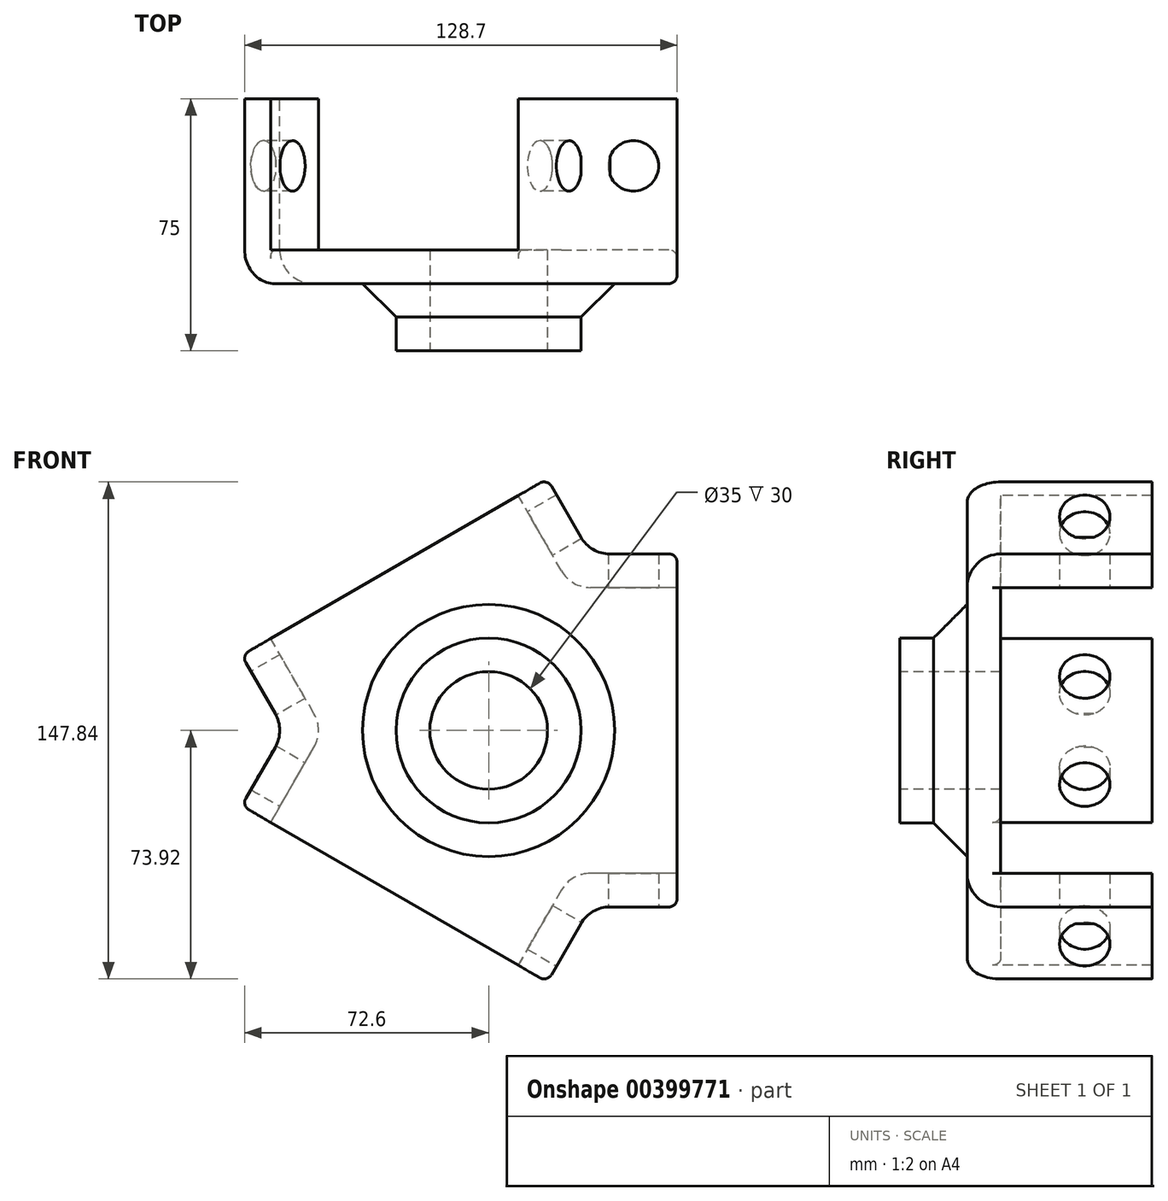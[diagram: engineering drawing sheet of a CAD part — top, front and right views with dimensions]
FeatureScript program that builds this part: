
annotation { "Feature Type Name" : "Feature", "Feature Type Description" : "" }
export const myFeature = defineFeature(function(context is Context, id is Id, definition is map)
    precondition{}
    {
        {
            var Q0;
            Q0=qCreatedBy(makeId("Front.planeOp"),FACE);
            var sketch = newSketch(context, id + "F0", { "sketchPlane" : qUnion([Q0])});
            skCircle(sketch, "E0", {"center": v(0, 0) * mm, "radius": 27.5 * mm});
            skCircle(sketch, "E1", {"center": v(0, 0) * mm, "radius": 17.5 * mm});
            skSolve(sketch);
        }
        {
            var Q0;
            Q0=makeQuery(id+"F0.imprint","IMPRINT",FACE,{"disambiguationData":[TD([[makeQuery(id+"F0.imprint","IMPRINT",EDGE,{"derivedFrom":sQuery(id+"F0.wireOp",EDGE,"E1")}),1.0]])]});
            var Q1;
            Q1=makeQuery(id+"F0.imprint","IMPRINT",FACE,{"disambiguationData":[TD([[makeQuery(id+"F0.imprint","IMPRINT",EDGE,{"derivedFrom":sQuery(id+"F0.wireOp",EDGE,"E0")}),1.0]])]});
            extrude(context, id + "F1", {"entities" : qUnion([Q0, Q1]), "oppositeDirection" : true, "depth" : 10 * mm});
        }
        {
            var Q0;
            Q0=makeQuery(id+"F1.opExtrude","CAP_FACE",FACE,{"disambiguationData":[OSD([sQuery(id+"F0.wireOp",EDGE,"E0"),sQuery(id+"F0.wireOp",EDGE,"E1")])],"isStart":false});
            cPlane(context, id + "F2", {"entities" : qUnion([Q0]), "cplaneType" : CPlaneType.OFFSET, "offset" : 10 * mm, "width" : 152.4 * mm, "height" : 152.4 * mm});
        }
        {
            var Q0;
            Q0=qCreatedBy(id+"F2.planeOp",FACE);
            var sketch = newSketch(context, id + "F3", { "sketchPlane" : qUnion([Q0])});
            skCircle(sketch, "E2", {"center": v(0, 0) * mm, "radius": 37.5 * mm});
            skSolve(sketch);
        }
        {
            var Q0;
            Q0=makeQuery(id+"F1.opExtrude","CAP_FACE",FACE,{"disambiguationData":[OSD([sQuery(id+"F0.wireOp",EDGE,"E0"),sQuery(id+"F0.wireOp",EDGE,"E1")])],"isStart":false});
            var sketch = newSketch(context, id + "F4", { "sketchPlane" : qUnion([Q0])});
            skCircle(sketch, "E3.0", {"center": v(0, 0) * mm, "radius": 27.5 * mm});
            skSolve(sketch);
        }
        {
            var Q1;
            Q1=makeQuery(id+"F4.imprint","IMPRINT",FACE,{"disambiguationData":[TD([[makeQuery(id+"F4.imprint","IMPRINT",EDGE,{"derivedFrom":sQuery(id+"F4.wireOp",EDGE,"E3.0")}),-1.0]])]});
            var Q2;
            Q2=makeQuery(id+"F3.imprint","IMPRINT",FACE,{"disambiguationData":[TD([[makeQuery(id+"F3.imprint","IMPRINT",EDGE,{"derivedFrom":sQuery(id+"F3.wireOp",EDGE,"E2")}),1.0]])]});
            loft(context, id + "F5", {"operationType" : NewBodyOperationType.ADD, "sheetProfilesArray" : [{ "sheetProfileEntities" : qUnion([Q1]) }, { "sheetProfileEntities" : qUnion([Q2]) }]});
        }
        {
            var Q0;
            Q0=makeQuery(id+"F5.opLoft","CAP_FACE",FACE,{"disambiguationData":[OSD([makeQuery(id+"F3.imprint","IMPRINT",FACE,{"disambiguationData":[TD([[makeQuery(id+"F3.imprint","IMPRINT",EDGE,{"derivedFrom":sQuery(id+"F3.wireOp",EDGE,"E2")}),1.0]])]})])],"isStart":true});
            var sketch = newSketch(context, id + "F6", { "sketchPlane" : qUnion([Q0])});
            skLineSegment(sketch, "E4", {"start": v(-103.3, 0) * mm, "end": v(129.97, 0) * mm, "construction": true});
            skLineSegment(sketch, "E5", {"start": v(0, 59.82) * mm, "end": v(0, -72.01) * mm, "construction": true});
            skLineSegment(sketch, "E6", {"start": v(-56.1, 52.5) * mm, "end": v(-56.1, -52.5) * mm});
            skLineSegment(sketch, "E7", {"start": v(-56.1, 52.5) * mm, "end": v(-30.31, 52.5) * mm});
            skLineSegment(sketch, "E8", {"start": v(-30.31, 52.5) * mm, "end": v(-17.42, 74.83) * mm});
            skLineSegment(sketch, "E9", {"start": v(-17.42, 74.83) * mm, "end": v(73.52, 22.33) * mm});
            skLineSegment(sketch, "E10", {"start": v(73.52, 22.33) * mm, "end": v(60.62, 0) * mm});
            skLineSegment(sketch, "E11", {"start": v(60.62, 0) * mm, "end": v(73.52, -22.33) * mm});
            skLineSegment(sketch, "E12", {"start": v(73.52, -22.33) * mm, "end": v(-17.42, -74.83) * mm});
            skLineSegment(sketch, "E13", {"start": v(-17.42, -74.83) * mm, "end": v(-30.31, -52.5) * mm});
            skLineSegment(sketch, "E14", {"start": v(-30.31, -52.5) * mm, "end": v(-56.1, -52.5) * mm});
            skSolve(sketch);
        }
        {
            var Q0;
            Q0 = qSketchRegion(id + "F6", true);
            extrude(context, id + "F7", {"entities" : qUnion([Q0]), "operationType" : NewBodyOperationType.ADD, "depth" : 10 * mm});
        }
        {
            var Q0;
            Q0=makeQuery(id+"F7.opExtrude","CAP_FACE",FACE,{"disambiguationData":[OSD([sQuery(id+"F6.wireOp",EDGE,"E6"),sQuery(id+"F6.wireOp",EDGE,"E7"),sQuery(id+"F6.wireOp",EDGE,"E8"),sQuery(id+"F6.wireOp",EDGE,"E9"),sQuery(id+"F6.wireOp",EDGE,"E10"),sQuery(id+"F6.wireOp",EDGE,"E11"),sQuery(id+"F6.wireOp",EDGE,"E12"),sQuery(id+"F6.wireOp",EDGE,"E13"),sQuery(id+"F6.wireOp",EDGE,"E14")])],"isStart":false});
            var sketch = newSketch(context, id + "F8", { "sketchPlane" : qUnion([Q0])});
            skLineSegment(sketch, "E15", {"start": v(-56.1, 52.5) * mm, "end": v(-56.1, 42.5) * mm});
            skLineSegment(sketch, "E16", {"start": v(-56.1, 42.5) * mm, "end": v(-24.54, 42.5) * mm});
            skLineSegment(sketch, "E17", {"start": v(-30.31, 52.5) * mm, "end": v(-56.1, 52.5) * mm});
            skLineSegment(sketch, "E18", {"start": v(-24.54, 42.5) * mm, "end": v(-8.76, 69.83) * mm});
            skLineSegment(sketch, "E19", {"start": v(-8.76, 69.83) * mm, "end": v(-17.42, 74.83) * mm});
            skLineSegment(sketch, "E20", {"start": v(-17.42, 74.83) * mm, "end": v(-30.31, 52.5) * mm});
            skLineSegment(sketch, "E21", {"start": v(-56.1, -52.5) * mm, "end": v(-56.1, -42.5) * mm});
            skLineSegment(sketch, "E22", {"start": v(-56.1, -42.5) * mm, "end": v(-24.54, -42.5) * mm});
            skLineSegment(sketch, "E23", {"start": v(-24.54, -42.5) * mm, "end": v(-8.76, -69.83) * mm});
            skLineSegment(sketch, "E24", {"start": v(-8.76, -69.83) * mm, "end": v(-17.42, -74.83) * mm});
            skLineSegment(sketch, "E25", {"start": v(-17.42, -74.83) * mm, "end": v(-30.31, -52.5) * mm});
            skLineSegment(sketch, "E26", {"start": v(-30.31, -52.5) * mm, "end": v(-56.1, -52.5) * mm});
            skLineSegment(sketch, "E27", {"start": v(73.52, -22.33) * mm, "end": v(64.86, -27.33) * mm});
            skLineSegment(sketch, "E28", {"start": v(64.86, -27.33) * mm, "end": v(49.07, 0) * mm});
            skLineSegment(sketch, "E29", {"start": v(49.07, 0) * mm, "end": v(64.86, 27.33) * mm});
            skLineSegment(sketch, "E30", {"start": v(64.86, 27.33) * mm, "end": v(73.52, 22.33) * mm});
            skLineSegment(sketch, "E31", {"start": v(73.52, 22.33) * mm, "end": v(60.62, 0) * mm});
            skLineSegment(sketch, "E32", {"start": v(60.62, 0) * mm, "end": v(73.52, -22.33) * mm});
            skLineSegment(sketch, "E33", {"start": v(64.86, -27.33) * mm, "end": v(73.52, -22.33) * mm});
            skSolve(sketch);
        }
        {
            var Q0;
            Q0 = qSketchRegion(id + "F8", true);
            extrude(context, id + "F9", {"entities" : qUnion([Q0]), "operationType" : NewBodyOperationType.ADD, "depth" : 45 * mm});
        }
        {
            var Q0;
            Q0=makeQuery(id+"F9.boolean.opBoolean","MERGE",EDGE,{"derivedFrom":[makeQuery(id+"F7.opExtrude","SWEPT_EDGE",EDGE,{"disambiguationData":[OSD([sQuery(id+"F6.wireOp",EDGE,"E10"),sQuery(id+"F6.wireOp",EDGE,"E11")])]}),makeQuery(id+"F9.opExtrude","SWEPT_EDGE",EDGE,{"disambiguationData":[OSD([sQuery(id+"F8.wireOp",EDGE,"E31"),sQuery(id+"F8.wireOp",EDGE,"E32")])]})]});
            var Q1;
            Q1=makeQuery(id+"F9.boolean.opBoolean","MERGE",EDGE,{"derivedFrom":[makeQuery(id+"F7.opExtrude","SWEPT_EDGE",EDGE,{"disambiguationData":[OSD([sQuery(id+"F6.wireOp",EDGE,"E7"),sQuery(id+"F6.wireOp",EDGE,"E8")])]}),makeQuery(id+"F9.opExtrude","SWEPT_EDGE",EDGE,{"disambiguationData":[OSD([sQuery(id+"F8.wireOp",EDGE,"E17"),sQuery(id+"F8.wireOp",EDGE,"E20")])]})]});
            var Q2;
            Q2=makeQuery(id+"F9.boolean.opBoolean","MERGE",EDGE,{"derivedFrom":[makeQuery(id+"F7.opExtrude","SWEPT_EDGE",EDGE,{"disambiguationData":[OSD([sQuery(id+"F6.wireOp",EDGE,"E13"),sQuery(id+"F6.wireOp",EDGE,"E14")])]}),makeQuery(id+"F9.opExtrude","SWEPT_EDGE",EDGE,{"disambiguationData":[OSD([sQuery(id+"F8.wireOp",EDGE,"E25"),sQuery(id+"F8.wireOp",EDGE,"E26")])]})]});
            var Q3;
            Q3=makeQuery(id+"F9.opExtrude","SWEPT_EDGE",EDGE,{"disambiguationData":[OSD([sQuery(id+"F8.wireOp",EDGE,"E22"),sQuery(id+"F8.wireOp",EDGE,"E23")])]});
            var Q4;
            Q4=makeQuery(id+"F9.opExtrude","SWEPT_EDGE",EDGE,{"disambiguationData":[OSD([sQuery(id+"F8.wireOp",EDGE,"E28"),sQuery(id+"F8.wireOp",EDGE,"E29")])]});
            var Q5;
            Q5=makeQuery(id+"F9.opExtrude","SWEPT_EDGE",EDGE,{"disambiguationData":[OSD([sQuery(id+"F8.wireOp",EDGE,"E16"),sQuery(id+"F8.wireOp",EDGE,"E18")])]});
            var Q6;
            Q6=makeQuery(id+"F9.opExtrude","CAP_EDGE",EDGE,{"disambiguationData":[OSD([sQuery(id+"F8.wireOp",EDGE,"E18")])],"isStart":true});
            var Q7;
            Q7=makeQuery(id+"F9.opExtrude","CAP_EDGE",EDGE,{"disambiguationData":[OSD([sQuery(id+"F8.wireOp",EDGE,"E23")])],"isStart":true});
            fillet(context, id + "F10", {"entities" : qUnion([Q0, Q1, Q2, Q3, Q4, Q5, Q6, Q7]), "radius" : 10 * mm, "tangentPropagation" : true, "allowEdgeOverflow" : false});
        }
        {
            var Q0;
            Q0=makeQuery(id+"F9.opExtrude","CAP_EDGE",EDGE,{"disambiguationData":[OSD([sQuery(id+"F8.wireOp",EDGE,"E29")])],"isStart":true});
            var Q1;
            Q1=makeQuery(id+"F7.opExtrude","CAP_EDGE",EDGE,{"disambiguationData":[OSD([sQuery(id+"F6.wireOp",EDGE,"E11")])],"isStart":true});
            var Q2;
            Q2=makeQuery(id+"F7.opExtrude","CAP_EDGE",EDGE,{"disambiguationData":[OSD([sQuery(id+"F6.wireOp",EDGE,"E13")])],"isStart":true});
            var Q3;
            Q3=makeQuery(id+"F7.opExtrude","CAP_EDGE",EDGE,{"disambiguationData":[OSD([sQuery(id+"F6.wireOp",EDGE,"E8")])],"isStart":true});
            fillet(context, id + "F11", {"entities" : qUnion([Q0, Q1, Q2, Q3]), "radius" : 10 * mm, "tangentPropagation" : true, "allowEdgeOverflow" : false});
        }
        {
            var Q0;
            Q0=makeQuery(id+"F7.opExtrude","CAP_EDGE",EDGE,{"disambiguationData":[OSD([sQuery(id+"F6.wireOp",EDGE,"E9")])],"isStart":true});
            var Q1;
            Q1=makeQuery(id+"F11.opFillet","BLEND_EDGE",EDGE,{"blendedFrom":[makeQuery(id+"F9.opExtrude","CAP_EDGE",EDGE,{"disambiguationData":[OSD([sQuery(id+"F8.wireOp",EDGE,"E29")])],"isStart":true}),makeQuery(id+"F9.boolean.opBoolean","MERGE",FACE,{"derivedFrom":[makeQuery(id+"F7.opExtrude","SWEPT_FACE",FACE,{"disambiguationData":[OSD([sQuery(id+"F6.wireOp",EDGE,"E9")])]}),makeQuery(id+"F9.opExtrude","SWEPT_FACE",FACE,{"disambiguationData":[OSD([sQuery(id+"F8.wireOp",EDGE,"E19")])]}),makeQuery(id+"F9.opExtrude","SWEPT_FACE",FACE,{"disambiguationData":[OSD([sQuery(id+"F8.wireOp",EDGE,"E30")])]})]})],"blendedInto":[makeQuery(id+"F9.boolean.opBoolean","MERGE",FACE,{"derivedFrom":[makeQuery(id+"F7.opExtrude","SWEPT_FACE",FACE,{"disambiguationData":[OSD([sQuery(id+"F6.wireOp",EDGE,"E9")])]}),makeQuery(id+"F9.opExtrude","SWEPT_FACE",FACE,{"disambiguationData":[OSD([sQuery(id+"F8.wireOp",EDGE,"E19")])]}),makeQuery(id+"F9.opExtrude","SWEPT_FACE",FACE,{"disambiguationData":[OSD([sQuery(id+"F8.wireOp",EDGE,"E30")])]})]})]});
            var Q2;
            Q2=makeQuery(id+"F7.opExtrude","CAP_EDGE",EDGE,{"disambiguationData":[OSD([sQuery(id+"F6.wireOp",EDGE,"E12")])],"isStart":true});
            var Q3;
            Q3=makeQuery(id+"F7.opExtrude","CAP_EDGE",EDGE,{"disambiguationData":[OSD([sQuery(id+"F6.wireOp",EDGE,"E12")])],"isStart":false});
            var Q4;
            Q4=makeQuery(id+"F7.opExtrude","CAP_EDGE",EDGE,{"disambiguationData":[OSD([sQuery(id+"F6.wireOp",EDGE,"E6")])],"isStart":false});
            var Q5;
            Q5=makeQuery(id+"F7.opExtrude","CAP_EDGE",EDGE,{"disambiguationData":[OSD([sQuery(id+"F6.wireOp",EDGE,"E6")])],"isStart":true});
            fillet(context, id + "F12", {"entities" : qUnion([Q0, Q1, Q2, Q3, Q4, Q5]), "radius" : 2.5 * mm, "tangentPropagation" : true, "allowEdgeOverflow" : false});
        }
        {
            var Q0;
            Q0=makeQuery(id+"F0.imprint","IMPRINT",FACE,{"disambiguationData":[TD([[makeQuery(id+"F0.imprint","IMPRINT",EDGE,{"derivedFrom":sQuery(id+"F0.wireOp",EDGE,"E1")}),1.0]])]});
            extrude(context, id + "F13", {"entities" : qUnion([Q0]), "operationType" : NewBodyOperationType.REMOVE, "oppositeDirection" : true, "depth" : 69.6 * mm});
        }
        {
            var Q0;
            Q0=makeQuery(id+"F9.opExtrude","SWEPT_FACE",FACE,{"disambiguationData":[OSD([sQuery(id+"F8.wireOp",EDGE,"E18")])]});
            var sketch = newSketch(context, id + "F14", { "sketchPlane" : qUnion([Q0])});
            skCircle(sketch, "E34", {"center": v(-55, 43.1) * mm, "radius": 7.5 * mm});
            skSolve(sketch);
        }
        {
            var Q0;
            Q0 = qSketchRegion(id + "F14", true);
            var Q1;
            Q1=makeQuery(id+"F9.boolean.opBoolean","MERGE",FACE,{"derivedFrom":[makeQuery(id+"F7.opExtrude","SWEPT_FACE",FACE,{"disambiguationData":[OSD([sQuery(id+"F6.wireOp",EDGE,"E8")])]}),makeQuery(id+"F9.opExtrude","SWEPT_FACE",FACE,{"disambiguationData":[OSD([sQuery(id+"F8.wireOp",EDGE,"E20")])]})]});
            var Q2;
            Q2=makeQuery(id+"F9.boolean.opBoolean","MERGE",FACE,{"derivedFrom":[makeQuery(id+"F7.opExtrude","SWEPT_FACE",FACE,{"disambiguationData":[OSD([sQuery(id+"F6.wireOp",EDGE,"E10")])]}),makeQuery(id+"F9.opExtrude","SWEPT_FACE",FACE,{"disambiguationData":[OSD([sQuery(id+"F8.wireOp",EDGE,"E31")])]})]});
            extrude(context, id + "F15", {"entities" : qUnion([Q0]), "operationType" : NewBodyOperationType.REMOVE, "endBound" : BoundingType.UP_TO_SURFACE, "oppositeDirection" : true, "endBoundEntityFace" : qUnion([Q1]), "depth" : 25.4 * mm, "hasSecondDirection" : true, "secondDirectionBound" : SecondDirectionBoundingType.UP_TO_SURFACE, "secondDirectionOppositeDirection" : false, "secondDirectionBoundEntityFace" : qUnion([Q2]), "secondDirectionDepth" : 25.4 * mm});
        }
        {
            var Q0;
            Q0=makeQuery(id+"F9.opExtrude","SWEPT_FACE",FACE,{"disambiguationData":[OSD([sQuery(id+"F8.wireOp",EDGE,"E16")])]});
            var sketch = newSketch(context, id + "F16", { "sketchPlane" : qUnion([Q0])});
            skCircle(sketch, "E35", {"center": v(43.1, -55) * mm, "radius": 7.5 * mm});
            skSolve(sketch);
        }
        {
            var Q0;
            Q0 = qSketchRegion(id + "F16", true);
            var Q1;
            Q1=makeQuery(id+"F9.boolean.opBoolean","MERGE",FACE,{"derivedFrom":[makeQuery(id+"F7.opExtrude","SWEPT_FACE",FACE,{"disambiguationData":[OSD([sQuery(id+"F6.wireOp",EDGE,"E7")])]}),makeQuery(id+"F9.opExtrude","SWEPT_FACE",FACE,{"disambiguationData":[OSD([sQuery(id+"F8.wireOp",EDGE,"E17")])]})]});
            var Q2;
            Q2=makeQuery(id+"F9.boolean.opBoolean","MERGE",FACE,{"derivedFrom":[makeQuery(id+"F7.opExtrude","SWEPT_FACE",FACE,{"disambiguationData":[OSD([sQuery(id+"F6.wireOp",EDGE,"E14")])]}),makeQuery(id+"F9.opExtrude","SWEPT_FACE",FACE,{"disambiguationData":[OSD([sQuery(id+"F8.wireOp",EDGE,"E26")])]})]});
            extrude(context, id + "F17", {"entities" : qUnion([Q0]), "operationType" : NewBodyOperationType.REMOVE, "endBound" : BoundingType.UP_TO_SURFACE, "oppositeDirection" : true, "endBoundEntityFace" : qUnion([Q1]), "depth" : 25.4 * mm, "hasSecondDirection" : true, "secondDirectionBound" : SecondDirectionBoundingType.UP_TO_SURFACE, "secondDirectionOppositeDirection" : false, "secondDirectionBoundEntityFace" : qUnion([Q2]), "secondDirectionDepth" : 25.4 * mm});
        }
        {
            var Q0;
            Q0=makeQuery(id+"F9.opExtrude","SWEPT_FACE",FACE,{"disambiguationData":[OSD([sQuery(id+"F8.wireOp",EDGE,"E28")])]});
            var sketch = newSketch(context, id + "F18", { "sketchPlane" : qUnion([Q0])});
            skCircle(sketch, "E36", {"center": v(55, -43.1) * mm, "radius": 7.5 * mm});
            skSolve(sketch);
        }
        {
            var Q0;
            Q0 = qSketchRegion(id + "F18", true);
            var Q1;
            Q1=makeQuery(id+"F9.boolean.opBoolean","MERGE",FACE,{"derivedFrom":[makeQuery(id+"F7.opExtrude","SWEPT_FACE",FACE,{"disambiguationData":[OSD([sQuery(id+"F6.wireOp",EDGE,"E11")])]}),makeQuery(id+"F9.opExtrude","SWEPT_FACE",FACE,{"disambiguationData":[OSD([sQuery(id+"F8.wireOp",EDGE,"E32")])]})]});
            var Q2;
            Q2=makeQuery(id+"F9.boolean.opBoolean","MERGE",FACE,{"derivedFrom":[makeQuery(id+"F7.opExtrude","SWEPT_FACE",FACE,{"disambiguationData":[OSD([sQuery(id+"F6.wireOp",EDGE,"E13")])]}),makeQuery(id+"F9.opExtrude","SWEPT_FACE",FACE,{"disambiguationData":[OSD([sQuery(id+"F8.wireOp",EDGE,"E25")])]})]});
            extrude(context, id + "F19", {"entities" : qUnion([Q0]), "operationType" : NewBodyOperationType.REMOVE, "endBound" : BoundingType.UP_TO_SURFACE, "oppositeDirection" : true, "endBoundEntityFace" : qUnion([Q1]), "depth" : 25.4 * mm, "hasSecondDirection" : true, "secondDirectionBound" : SecondDirectionBoundingType.UP_TO_SURFACE, "secondDirectionOppositeDirection" : false, "secondDirectionBoundEntityFace" : qUnion([Q2]), "secondDirectionDepth" : 25.4 * mm});
        }
    });
